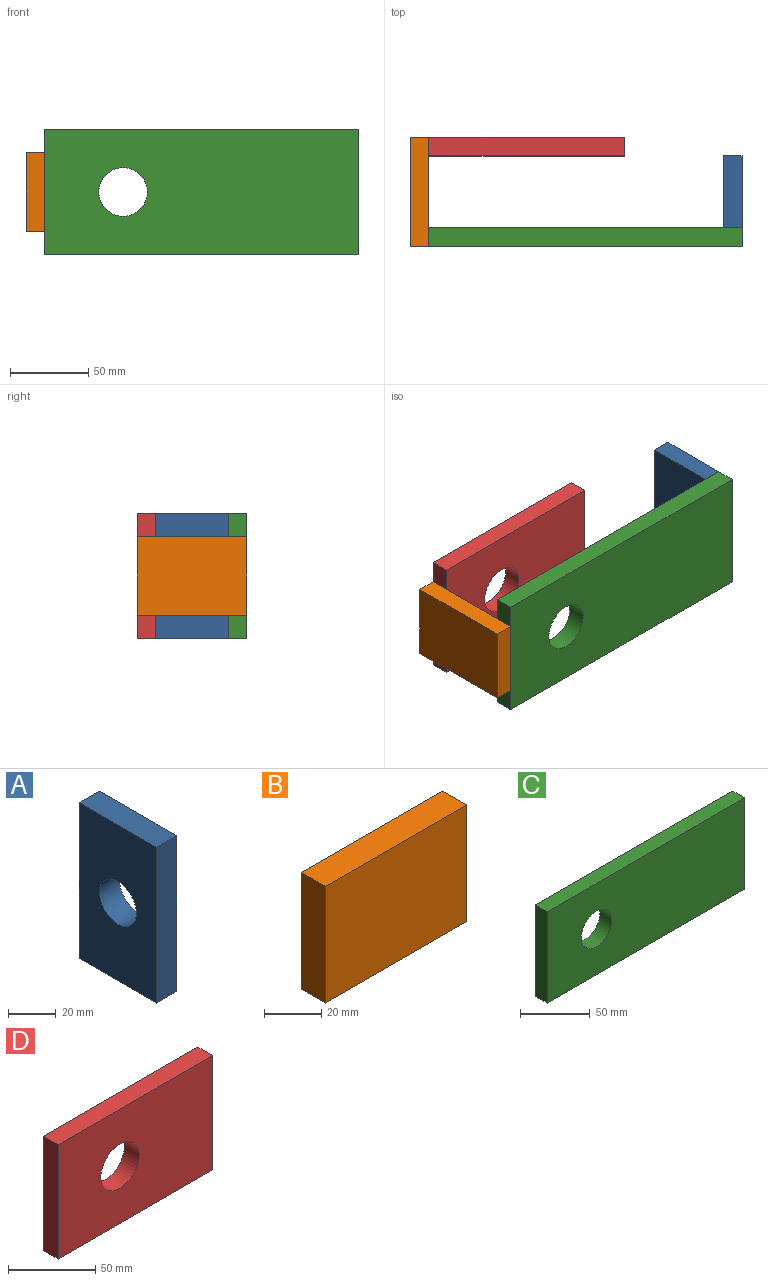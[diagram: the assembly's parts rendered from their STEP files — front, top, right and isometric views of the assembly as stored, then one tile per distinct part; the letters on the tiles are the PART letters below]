
ASSEMBLY  parts=4 mates=3
PART A: 7 faces, bbox 12x46x80 mm
  f0: plane 46x12mm, normal (0,0,-1), area 552mm2, adj f1,f4,f5,f6
  f1: plane 80x12mm, normal (0,1,0), area 960mm2, adj f0,f2,f5,f6
  f2: plane 46x12mm, normal (0,0,1), area 552mm2, adj f1,f4,f5,f6
  f3: cylinder r=11mm len=22mm, axis (-1,0,0), area 829.4mm2, adj f5,f6
  f4: plane 80x12mm, normal (0,-1,0), area 960mm2, adj f0,f2,f5,f6
  f5: plane 80x46mm, normal (1,0,0), area 3299.9mm2, adj f0,f1,f2,f3,f4
  f6: plane 80x46mm, normal (-1,0,0), area 3299.9mm2, adj f0,f1,f2,f3,f4
PART B: 6 faces, bbox 70x12x50 mm
  f0: plane 70x12mm, normal (0,0,-1), area 840mm2, adj f1,f3,f4,f5
  f1: plane 50x12mm, normal (1,0,0), area 600mm2, adj f0,f2,f4,f5
  f2: plane 70x12mm, normal (0,0,1), area 840mm2, adj f1,f3,f4,f5
  f3: plane 50x12mm, normal (-1,0,0), area 600mm2, adj f0,f2,f4,f5
  f4: plane 70x50mm, normal (0,-1,0), area 3500mm2, adj f0,f1,f2,f3
  f5: plane 70x50mm, normal (0,1,0), area 3500mm2, adj f0,f1,f2,f3
PART C: 7 faces, bbox 200x12x80 mm
  f0: plane 200x12mm, normal (0,0,-1), area 2400mm2, adj f1,f3,f5,f6
  f1: plane 80x12mm, normal (1,0,0), area 960mm2, adj f0,f2,f5,f6
  f2: plane 200x12mm, normal (0,0,1), area 2400mm2, adj f1,f3,f5,f6
  f3: plane 80x12mm, normal (-1,0,0), area 960mm2, adj f0,f2,f5,f6
  f4: cylinder r=15.5mm len=31mm, axis (0,1,0), area 1168.7mm2, adj f5,f6
  f5: plane 200x80mm, normal (0,-1,0), area 15245.2mm2, adj f0,f1,f2,f3,f4
  f6: plane 200x80mm, normal (0,1,0), area 15245.2mm2, adj f0,f1,f2,f3,f4
PART D: 7 faces, bbox 125x12x80 mm
  f0: plane 125x12mm, normal (0,0,-1), area 1500mm2, adj f1,f3,f5,f6
  f1: plane 80x12mm, normal (1,0,0), area 960mm2, adj f0,f2,f5,f6
  f2: plane 125x12mm, normal (0,0,1), area 1500mm2, adj f1,f3,f5,f6
  f3: plane 80x12mm, normal (-1,0,0), area 960mm2, adj f0,f2,f5,f6
  f4: cylinder r=15.5mm len=31mm, axis (0,1,0), area 1168.7mm2, adj f5,f6
  f5: plane 125x80mm, normal (0,-1,0), area 9245.2mm2, adj f0,f1,f2,f3,f4
  f6: plane 125x80mm, normal (0,1,0), area 9245.2mm2, adj f0,f1,f2,f3,f4
PLACE A t=(80.49,11.29,-2.05)mm
PLACE B rot(axis=(0,0,1),90deg) t=(-119.51,11.29,-2.05)mm
PLACE C t=(-7.51,-11.71,-2.05)mm
PLACE D t=(-45.01,46.29,-2.05)mm
MATE fastened A.f4 <-> C.f6  axis (0,-1,0) through (92.49,-11.71,-2.05)mm
MATE fastened D.f3 <-> B.f4  axis (-1,0,0) through (-107.51,46.29,-2.05)mm
MATE fastened B.f4 <-> C.f3  axis (1,0,0) through (-107.51,-23.71,-2.05)mm
